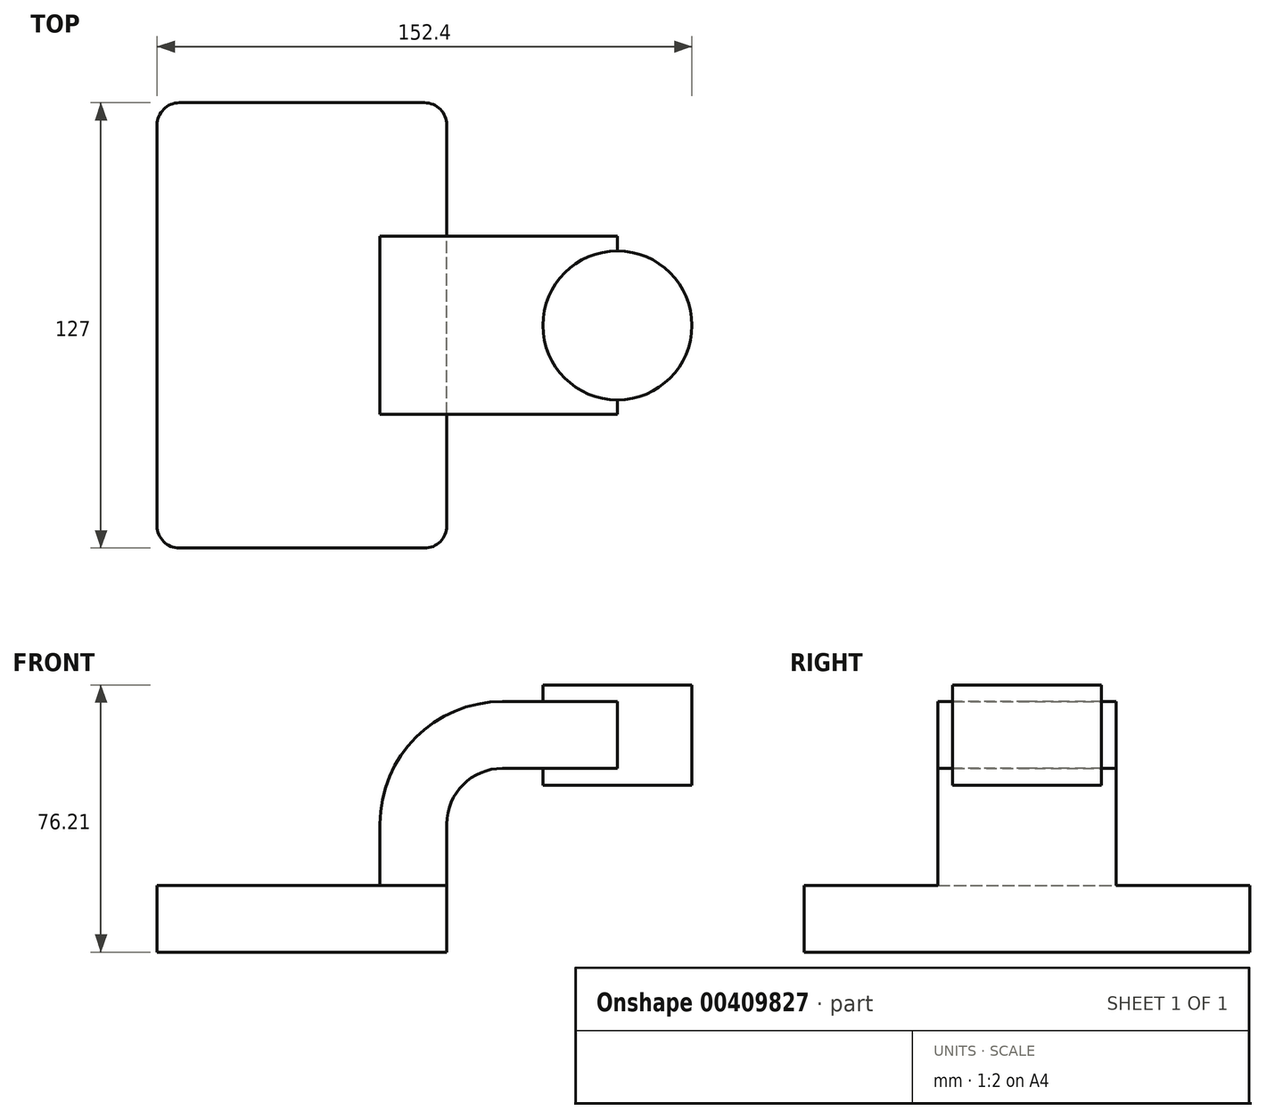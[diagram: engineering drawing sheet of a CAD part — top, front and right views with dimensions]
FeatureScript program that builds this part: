
annotation { "Feature Type Name" : "Feature", "Feature Type Description" : "" }
export const myFeature = defineFeature(function(context is Context, id is Id, definition is map)
    precondition{}
    {
        {
            var Q0;
            Q0=qCreatedBy(makeId("Front.planeOp"),FACE);
            var sketch = newSketch(context, id + "F0", { "sketchPlane" : qUnion([Q0])});
            skLineSegment(sketch, "E0.bottom", {"start": v(41.27, 9.53) * mm, "end": v(-41.28, 9.53) * mm});
            skLineSegment(sketch, "E0.top", {"start": v(41.28, -9.52) * mm, "end": v(-41.27, -9.53) * mm});
            skLineSegment(sketch, "E0.left", {"start": v(41.27, 9.53) * mm, "end": v(41.28, -9.52) * mm});
            skLineSegment(sketch, "E0.right", {"start": v(-41.28, 9.53) * mm, "end": v(-41.27, -9.53) * mm});
            skPoint(sketch, "E0.middle", {"position": v(0, 0) * mm});
            skLineSegment(sketch, "E1.bottom", {"start": v(111.12, 38.1) * mm, "end": v(60.32, 38.1) * mm});
            skLineSegment(sketch, "E1.top", {"start": v(111.12, 66.68) * mm, "end": v(60.32, 66.68) * mm});
            skLineSegment(sketch, "E1.left", {"start": v(111.12, 38.1) * mm, "end": v(111.12, 66.68) * mm});
            skLineSegment(sketch, "E1.right", {"start": v(60.32, 38.1) * mm, "end": v(60.32, 66.68) * mm});
            skPoint(sketch, "E1.middle", {"position": v(85.72, 52.39) * mm});
            skLineSegment(sketch, "E2", {"start": v(41.27, 9.53) * mm, "end": v(41.27, 27) * mm});
            skArc(sketch, "E3", {"start": v(41.27, 27) * mm, "mid": v(45.92, 38.23) * mm, "end": v(57.15, 42.88) * mm});
            skLineSegment(sketch, "E4", {"start": v(57.15, 42.88) * mm, "end": v(89.89, 42.88) * mm});
            skLineSegment(sketch, "E5.0", {"start": v(57.15, 61.93) * mm, "end": v(89.89, 61.93) * mm});
            skArc(sketch, "E5.1", {"start": v(22.22, 27) * mm, "mid": v(32.45, 51.7) * mm, "end": v(57.15, 61.93) * mm});
            skLineSegment(sketch, "E5.2", {"start": v(22.22, 9.53) * mm, "end": v(22.22, 27) * mm});
            skLineSegment(sketch, "E6", {"start": v(89.89, 38.1) * mm, "end": v(89.89, 66.68) * mm});
            skFitSpline(sketch, "E7", {"points": [v(-41.27, 9.52) * mm, v(57.15, 61.93) * mm], "startDerivative": vector(27.07, 92.26) * mm, "endDerivative": vector(109.97, -13.8) * mm});
            skSolve(sketch);
        }
        {
            var Q0;
            Q0=makeQuery(id+"F0.imprint","IMPRINT",FACE,{"disambiguationData":[TD([[makeQuery(id+"F0.imprint","IMPRINT",EDGE,{"derivedFrom":sQuery(id+"F0.wireOp",EDGE,"E0.top")}),-1.0]])]});
            extrude(context, id + "F1", {"entities" : qUnion([Q0]), "endBound" : BoundingType.SYMMETRIC, "depth" : 127 * mm});
        }
        {
            var Q0;
            {var subQ1=sQuery(id+"F0.wireOp",EDGE,"E2");Q0=makeQuery(id+"F0.imprint","IMPRINT",FACE,{"disambiguationData":[TD([[makeQuery(id+"F0.imprint","IMPRINT",EDGE,{"derivedFrom":subQ1}),1.0]])]});}
            var Q1;
            {var subQ0=sQuery(id+"F0.wireOp",EDGE,"E4");var subQ1=sQuery(id+"F0.wireOp",EDGE,"E1.right");var subQ2=makeQuery(id+"F0.imprint","INTERSECT",VERTEX,{"derivedFrom":[subQ1,subQ0]});Q1=makeQuery(id+"F0.imprint","IMPRINT",FACE,{"disambiguationData":[TD([[makeQuery(id+"F0.imprint","IMPRINT",EDGE,{"disambiguationData":[TD([[subQ2,-1.0]])],"derivedFrom":subQ1}),-1.0]])]});}
            extrude(context, id + "F2", {"entities" : qUnion([Q0, Q1]), "operationType" : NewBodyOperationType.ADD, "endBound" : BoundingType.SYMMETRIC, "depth" : 50.8 * mm});
        }
        {
            var Q0;
            Q0=makeQuery(id+"F0.imprint","IMPRINT",FACE,{"disambiguationData":[TD([[makeQuery(id+"F0.imprint","IMPRINT",EDGE,{"derivedFrom":sQuery(id+"F0.wireOp",EDGE,"E5.1")}),1.0]])]});
            extrude(context, id + "F3", {"entities" : qUnion([Q0]), "operationType" : NewBodyOperationType.ADD, "endBound" : BoundingType.UP_TO_NEXT, "depth" : 15.88 * mm});
        }
        {
            var Q0;
            {var subQ4=sQuery(id+"F0.wireOp",EDGE,"E1.left");Q0=makeQuery(id+"F0.imprint","IMPRINT",FACE,{"disambiguationData":[TD([[makeQuery(id+"F0.imprint","IMPRINT",EDGE,{"derivedFrom":subQ4}),1.0]])]});}
            var Q1;
            Q1=sQuery(id+"F0.wireOp",EDGE,"E6");
            revolve(context, id + "F4", {"operationType" : NewBodyOperationType.ADD, "entities" : qUnion([Q0]), "axis" : qUnion([Q1]), "revolveType" : RevolveType.FULL});
        }
        {
            var Q0;
            Q0=makeQuery(id+"F1.opExtrude","CAP_EDGE",EDGE,{"disambiguationData":[OSD([sQuery(id+"F0.wireOp",EDGE,"E0.left")])],"isStart":false});
            var Q1;
            Q1=makeQuery(id+"F1.opExtrude","CAP_EDGE",EDGE,{"disambiguationData":[OSD([sQuery(id+"F0.wireOp",EDGE,"E0.right")])],"isStart":false});
            var Q2;
            Q2=makeQuery(id+"F1.opExtrude","CAP_EDGE",EDGE,{"disambiguationData":[OSD([sQuery(id+"F0.wireOp",EDGE,"E0.left")])],"isStart":true});
            var Q3;
            Q3=makeQuery(id+"F1.opExtrude","CAP_EDGE",EDGE,{"disambiguationData":[OSD([sQuery(id+"F0.wireOp",EDGE,"E0.right")])],"isStart":true});
            fillet(context, id + "F5", {"entities" : qUnion([Q0, Q1, Q2, Q3]), "radius" : 6.35 * mm, "tangentPropagation" : true, "allowEdgeOverflow" : false});
        }
    });
